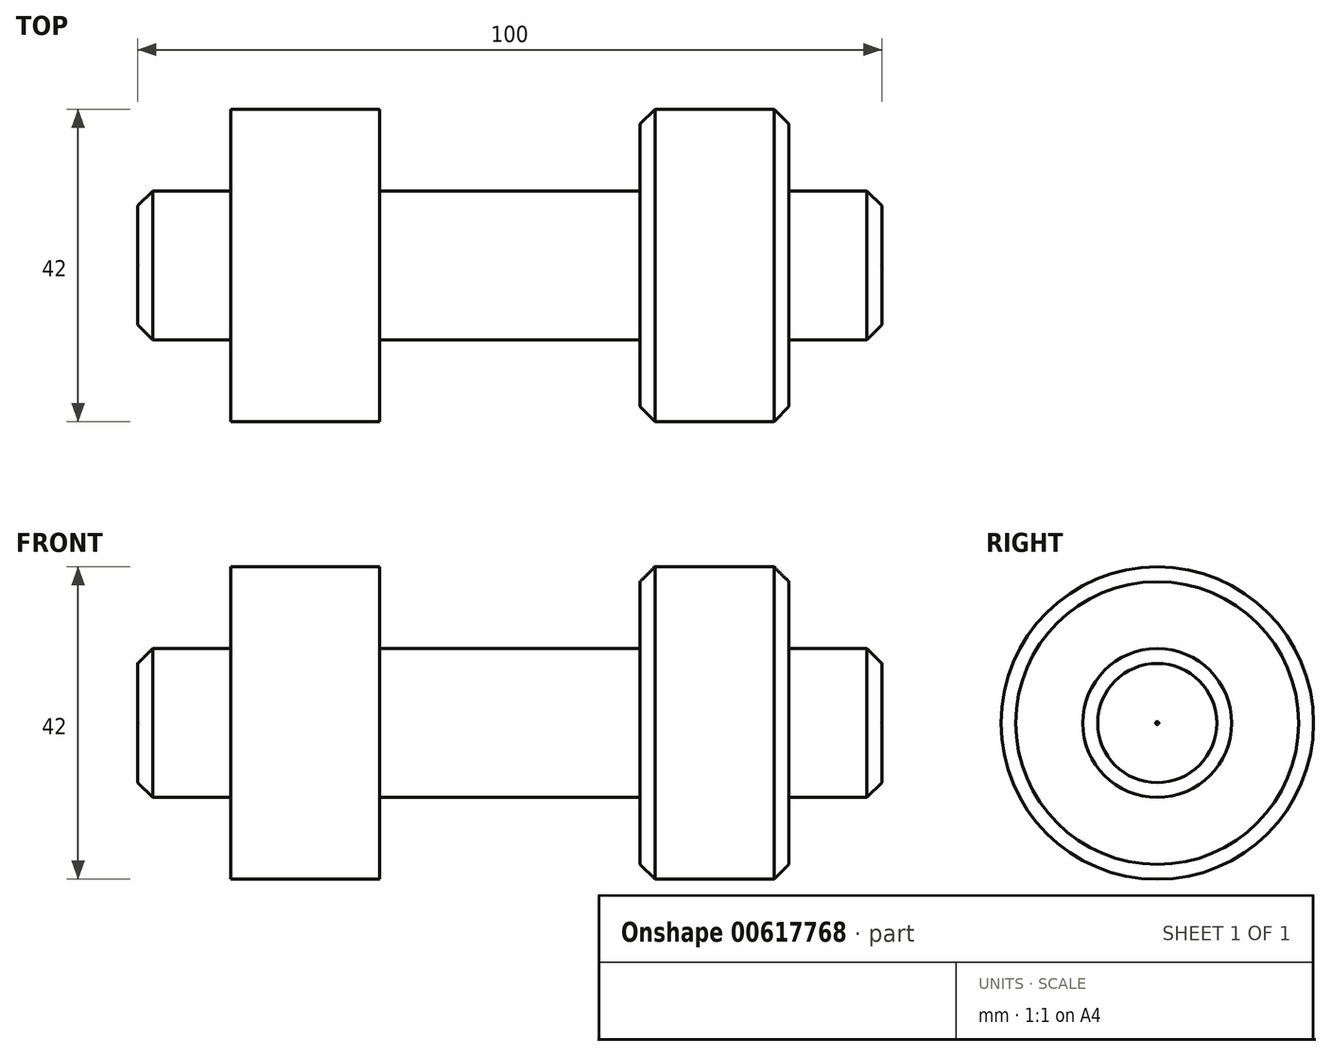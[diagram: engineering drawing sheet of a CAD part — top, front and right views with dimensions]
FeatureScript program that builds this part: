
annotation { "Feature Type Name" : "Feature", "Feature Type Description" : "" }
export const myFeature = defineFeature(function(context is Context, id is Id, definition is map)
    precondition{}
    {
        {
            var Q0;
            Q0=qCreatedBy(makeId("Front.planeOp"),FACE);
            var sketch = newSketch(context, id + "F0", { "sketchPlane" : qUnion([Q0])});
            skLineSegment(sketch, "E0.bottom", {"start": v(0, 0) * mm, "end": v(12.5, 0) * mm});
            skLineSegment(sketch, "E0.top", {"start": v(0, -10) * mm, "end": v(12.5, -10) * mm});
            skLineSegment(sketch, "E0.left", {"start": v(0, 0) * mm, "end": v(0, -10) * mm});
            skLineSegment(sketch, "E0.right", {"start": v(12.5, 0) * mm, "end": v(12.5, -10) * mm});
            skLineSegment(sketch, "E1.bottom", {"start": v(12.5, 0) * mm, "end": v(32.5, 0) * mm});
            skLineSegment(sketch, "E1.top", {"start": v(12.5, -21) * mm, "end": v(32.5, -21) * mm});
            skLineSegment(sketch, "E1.left", {"start": v(12.5, 0) * mm, "end": v(12.5, -21) * mm});
            skLineSegment(sketch, "E1.right", {"start": v(32.5, 0) * mm, "end": v(32.5, -21) * mm});
            skLineSegment(sketch, "E2.bottom", {"start": v(32.5, 0) * mm, "end": v(67.5, 0) * mm});
            skLineSegment(sketch, "E2.top", {"start": v(32.5, -10) * mm, "end": v(67.5, -10) * mm});
            skLineSegment(sketch, "E2.left", {"start": v(32.5, 0) * mm, "end": v(32.5, -10) * mm});
            skLineSegment(sketch, "E2.right", {"start": v(67.5, 0) * mm, "end": v(67.5, -10) * mm});
            skLineSegment(sketch, "E3", {"start": v(50, 13.15) * mm, "end": v(50, 30.51) * mm});
            skPoint(sketch, "E3.startSnap0", {"position": v(50, 0) * mm});
            skLineSegment(sketch, "E4.MirrorCS", {"start": v(67.5, 0) * mm, "end": v(67.5, -21) * mm});
            skLineSegment(sketch, "E5.MirrorCS", {"start": v(87.5, 0) * mm, "end": v(67.5, 0) * mm});
            skLineSegment(sketch, "E6.MirrorCS", {"start": v(87.5, 0) * mm, "end": v(87.5, -21) * mm});
            skLineSegment(sketch, "E7.MirrorCS", {"start": v(100, -10) * mm, "end": v(87.5, -10) * mm});
            skLineSegment(sketch, "E8.MirrorCS", {"start": v(100, 0) * mm, "end": v(87.5, 0) * mm});
            skLineSegment(sketch, "E9.MirrorCS", {"start": v(100, 0) * mm, "end": v(100, -10) * mm});
            skLineSegment(sketch, "E10.MirrorCS", {"start": v(87.5, -21) * mm, "end": v(67.5, -21) * mm});
            skLineSegment(sketch, "E11", {"start": v(0, -0.2) * mm, "end": v(0.2, 0) * mm});
            skLineSegment(sketch, "E12.MirrorCS", {"start": v(100, -0.2) * mm, "end": v(99.8, 0) * mm});
            skSolve(sketch);
        }
        {
            var Q0;
            {var subQ3=sQuery(id+"F0.wireOp",EDGE,"E1.bottom");Q0=makeQuery(id+"F0.imprint","IMPRINT",FACE,{"disambiguationData":[TD([[makeQuery(id+"F0.imprint","IMPRINT",EDGE,{"derivedFrom":subQ3}),-1.0]])]});}
            var Q1;
            {var subQ2=sQuery(id+"F0.wireOp",EDGE,"E7.MirrorCS");Q1=makeQuery(id+"F0.imprint","IMPRINT",FACE,{"disambiguationData":[TD([[makeQuery(id+"F0.imprint","IMPRINT",EDGE,{"derivedFrom":subQ2}),-1.0]])]});}
            var Q2;
            {var subQ1=sQuery(id+"F0.wireOp",EDGE,"E5.MirrorCS");Q2=makeQuery(id+"F0.imprint","IMPRINT",FACE,{"disambiguationData":[TD([[makeQuery(id+"F0.imprint","IMPRINT",EDGE,{"derivedFrom":subQ1}),1.0]])]});}
            var Q3;
            {var subQ0=sQuery(id+"F0.wireOp",EDGE,"E2.bottom");Q3=makeQuery(id+"F0.imprint","IMPRINT",FACE,{"disambiguationData":[TD([[makeQuery(id+"F0.imprint","IMPRINT",EDGE,{"derivedFrom":subQ0}),-1.0]])]});}
            var Q4;
            {var subQ1=sQuery(id+"F0.wireOp",EDGE,"E0.top");Q4=makeQuery(id+"F0.imprint","IMPRINT",FACE,{"disambiguationData":[TD([[makeQuery(id+"F0.imprint","IMPRINT",EDGE,{"derivedFrom":subQ1}),1.0]])]});}
            var Q5;
            Q5=sQuery(id+"F0.wireOp",EDGE,"E2.bottom");
            revolve(context, id + "F1", {"entities" : qUnion([Q0, Q1, Q2, Q3, Q4]), "axis" : qUnion([Q5]), "revolveType" : RevolveType.FULL});
        }
        {
            var Q0;
            Q0=makeQuery(id+"F1.opRevolve","SWEPT_EDGE",EDGE,{"disambiguationData":[OSD([sQuery(id+"F0.wireOp",EDGE,"E4.MirrorCS"),sQuery(id+"F0.wireOp",EDGE,"E10.MirrorCS")])]});
            var Q1;
            Q1=makeQuery(id+"F1.opRevolve","SWEPT_EDGE",EDGE,{"disambiguationData":[OSD([sQuery(id+"F0.wireOp",EDGE,"E6.MirrorCS"),sQuery(id+"F0.wireOp",EDGE,"E10.MirrorCS")])]});
            var Q2;
            Q2=makeQuery(id+"F1.opRevolve","SWEPT_EDGE",EDGE,{"disambiguationData":[OSD([sQuery(id+"F0.wireOp",EDGE,"E7.MirrorCS"),sQuery(id+"F0.wireOp",EDGE,"E9.MirrorCS")])]});
            var Q3;
            Q3=makeQuery(id+"F1.opRevolve","SWEPT_EDGE",EDGE,{"disambiguationData":[OSD([sQuery(id+"F0.wireOp",EDGE,"E0.top"),sQuery(id+"F0.wireOp",EDGE,"E0.left")])]});
            chamfer(context, id + "F2", {"entities" : qUnion([Q0, Q1, Q2, Q3]), "width" : 2 * mm, "tangentPropagation" : true});
        }
    });
